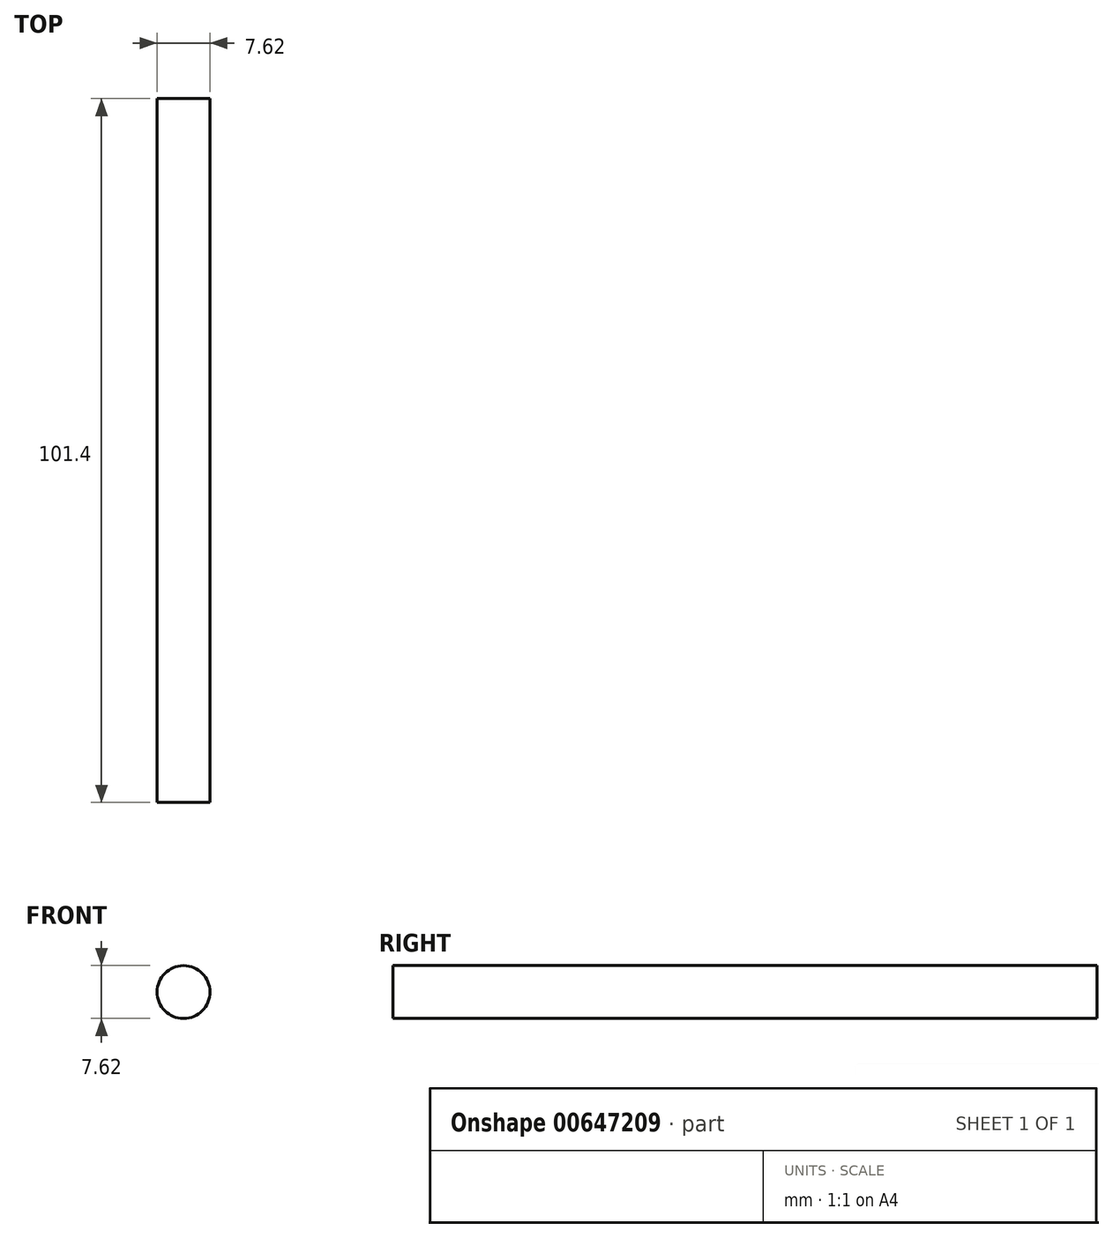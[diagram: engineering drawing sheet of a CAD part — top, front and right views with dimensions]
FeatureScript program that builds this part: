
annotation { "Feature Type Name" : "Feature", "Feature Type Description" : "" }
export const myFeature = defineFeature(function(context is Context, id is Id, definition is map)
    precondition{}
    {
        {
            var Q0;
            Q0=qCreatedBy(makeId("Front.planeOp"),FACE);
            var sketch = newSketch(context, id + "F0", { "sketchPlane" : qUnion([Q0])});
            skCircle(sketch, "E0", {"center": v(0, 0) * mm, "radius": 3.81 * mm});
            skSolve(sketch);
        }
        {
            var Q0;
            Q0 = qSketchRegion(id + "F0", true);
            extrude(context, id + "F1", {"entities" : qUnion([Q0]), "oppositeDirection" : true, "depth" : 50.7 * mm, "offsetDistance" : 25.4 * mm, "hasSecondDirection" : true, "secondDirectionOppositeDirection" : false, "secondDirectionDepth" : 50.7 * mm});
        }
    });
